# Revit family: Condensing-Solar-Storage-Water-Heater-Gas_AO_Smith-SGS_28_F
name_source: partatom
category: Mechanical Equipment
revit_build: Autodesk Revit 2014 (Build: 20130308_1515(x64)
units: mm (PartAtom-declared; Revit-internal decimal feet)

## types (1)
- Condensing-Solar-Storage-Water-Heater-Gas_AO_Smith-SGS_28_F
    (Contrôle supplémentaires) Fréquence secteur (± 1 Hz) = 50 Hz
    (Contrôle supplémentaires) Phase = 1
    (Contrôle supplémentaires) Puissance Électrique Absorbée = 700 W
    (Contrôle supplémentaires) Tension d'Alimentation (-15%, +10%) = 230 V
    1er Entretien (check-up) = 3 mois après l'installation
    2ème Entretien (Entretien Général) = 12 mois après l'installation
    Assembly Code = D3010
    BIM Content Developer = CAD & Company
    CE-PIN = 0063BU3889
    CO2-émissions (tol. ± 1.0) = 9.00/9.20
    Capacité = 217.0 L
    Catégorie de Gaz = II2Esi3P
    Charge Maximale au Sol = 394 kg
    Charge Nominale (Valeur Inférieure) = 29000 W
    Charge Nominale (Valeur Supérieure) = 3200 W
    Consommation de Gaz - Masse = 0
    Consommation de Gaz - Volume = 3.10/3.60
    Description = Préparateur ECS Solaire en Combinaison avec Réservoir de Stockage
    Destination / Pays = France
    Diamètre = 705 mm
    Diamètre Cheminée - Boiler = 100/150 mm/mm
    Diamètre Cheminée - Système Concentrique = 100/150 mm/mm
    Diamètre Cheminée - Système Parallèle = 100 mm  [stored 0.328084 ft]
    Débit de vidage en Continu à ΔT = 28°C = 960.0 L/s
    Débit de vidage en Continu à ΔT = 44°C = 610.0 L/s
    Débit de vidage en Continu à ΔT = 50°C = 540.0 L/s
    Débit de vidage en Continu à ΔT = 55°C = 490.0 L/s
    Débit de vidage en Continu à ΔT = 70°C = 0.0 L/s
    Débit de vidage à ΔT = 28°C après 120 min. = 2100.0 L
    Débit de vidage à ΔT = 28°C après 30 min. = 650.0 L
    Débit de vidage à ΔT = 28°C après 60 min. = 1200.0 L
    Débit de vidage à ΔT = 28°C après 90 min. = 1700.0 L
    Débit de vidage à ΔT = 44°C après 120 min. = 1300.0 L
    Débit de vidage à ΔT = 44°C après 30 min. = 370.0 L
    Débit de vidage à ΔT = 44°C après 60 min. = 670.0 L
    Débit de vidage à ΔT = 44°C après 90 min. = 980.0 L
    Débit de vidage à ΔT = 50°C après 120 min. = 1200.0 L
    Débit de vidage à ΔT = 50°C après 30 min. = 310.0 L
    Débit de vidage à ΔT = 50°C après 60 min. = 570.0 L
    Débit de vidage à ΔT = 50°C après 90 min. = 840.0 L
    Débit de vidage à ΔT = 55°C après 120 min. = 990.0 L
    Débit de vidage à ΔT = 55°C après 30 min. = 260.0 L
    Débit de vidage à ΔT = 55°C après 60 min. = 500.0 L
    Débit de vidage à ΔT = 55°C après 90 min. = 750.0 L
    Débit de vidage à ΔT = 70°C après 120 min. = 0.0 L
    Débit de vidage à ΔT = 70°C après 30 min. = 0.0 L
    Débit de vidage à ΔT = 70°C après 60 min. = 0.0 L
    Débit de vidage à ΔT = 70°C après 90 min. = 0.0 L
    Epaisseur d'Isolation = 50 mm  [stored 0.164042 ft]
    Fabricant No. = E 7110
    Fréquence secteur (± 1 Hz) = 50 Hz
    Garantie Pièces = 12 mois
    Garantie sur la Cuve = 36 mois
    Guide de Produit = https://www.aosmithinternational.com
    Hauteur = 1485 mm
    Hauteur Conduit d'Alimentation en Air = 1460 mm
    Hauteur Conduit d'Évacuation des Fumées = 1460 mm
    Hauteur d'Emballage = 1550 mm
    Hauteur de l'Alimentation en eau Froide = 265 mm  [stored 0.869423 ft]
    Hauteur de la Sortie d'eau Chaude = 1485 mm
    Hauteur du Raccordement au Gaz = 1380 mm
    Largeur = 850 mm
    Largeur d'Emballage = 870 mm  [stored 2.85433 ft]
    Manufacturer = A.O. Smith Water Products Company b.v.
    Model = SGS 28 F
    NOX-émissions = 54.0/49.0
    NOX-émissions (ven air, 0% O2) = 30.0/27.0
    Niveau du Son = 45
    Nombre de modèle du produit (EAN) = 8,71745E+12
    Pertes en Veille = 0 W
    Pertes en Veille - tous les jours (24h) = 0 W
    Phase = 1
    Poids de Transport = 222 kg
    Poids à vide = 202 kg
    Pression Amont de Gaz = 2000/2500
    Pression Différentielle d'Ouverture de l'Interrupteur de Pression = 115.0 Pa
    Pression de Fonctionnement Maximale = 800000.0 Pa
    Production Nominale = 31000 W
    Profondeur = 925 mm
    Profondeur d'Emballage = 950 mm
    Puissance Électrique Absorbée = 45 W
    Raccord Robinet de Vidange = 1"
    Raccord d'Alimentation en Eau Froide = 1 1/2"
    Raccord de Gaz = 3/4"
    Raccord de Sortie d'Eau Chaude = 1 1/2"
    Raccord de la Soupape de Vidange = 1"
    Raccord Évacuation de la Condensation = 40 mm  [stored 0.131234 ft]
    Rendement (Hi, acc. NEN-EN 89 - 1999) = 107
    Rendement (Hs, acc. NEN-EN 89 - 1999) = 96
    Rendement Saisonnier (Hs) = 96
    Réglage Standard Pour = G20/G25
    Spécifications du Produit = https://www.aosmithinternational.com
    Temps de réchauffement à ΔT = 28°C = 14
    Temps de réchauffement à ΔT = 44°C = 21
    Temps de réchauffement à ΔT = 50°C = 24
    Temps de réchauffement à ΔT = 55°C = 27
    Température Maximale des Fumées = 45 °C
    Tension d'Alimentation (-15%, +10%) = 230 V
    Type d'Emballage = Plastique Emballage Rétractable, Carton et Bois
    Type d'Installation = B23/C13/C33/C43/C53/C63
    URL = http://www.aosmith.fr
    Valeur Défaut du Thermostat de Régulation = 65 °C
    Valeur Manimale du Thermostat de Régulation = 40 °C
    Valeur Maximale du Thermostat de Régulation = 80 °C
    l'Intervalle d'Entretien = 12 mois

note: [stored X ft] marks values corroborated as IEEE doubles in the binary element streams (Revit-internal decimal feet)

## geometry (parser evidence)
native form markers: Blend x19, Sweep x34
no freeform markers — native parametric forms only
